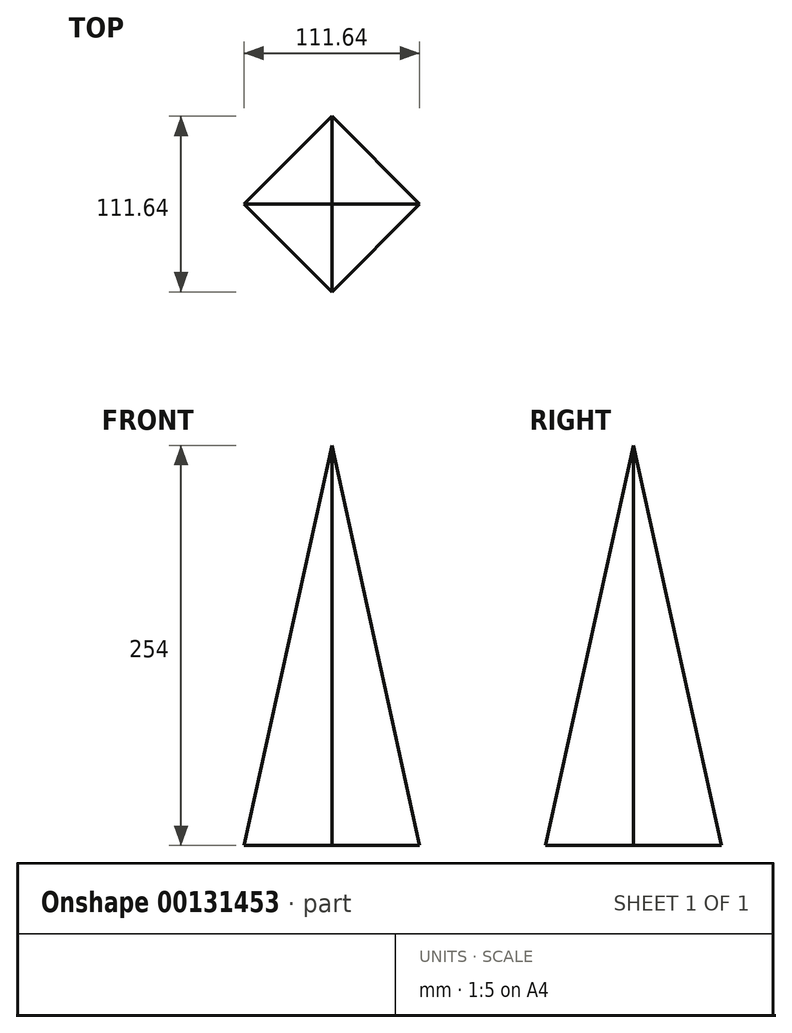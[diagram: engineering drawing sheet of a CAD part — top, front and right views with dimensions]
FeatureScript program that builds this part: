
annotation { "Feature Type Name" : "Feature", "Feature Type Description" : "" }
export const myFeature = defineFeature(function(context is Context, id is Id, definition is map)
    precondition{}
    {
        {
            var Q0;
            Q0=qCreatedBy(makeId("Top.planeOp"),FACE);
            var sketch = newSketch(context, id + "F0", { "sketchPlane" : qUnion([Q0])});
            skCircle(sketch, "E0.cCircle", {"center": v(0, 0) * mm, "radius": 55.82 * mm, "construction": true});
            skLineSegment(sketch, "E0.0", {"start": v(-55.82, 0) * mm, "end": v(0, 55.82) * mm});
            skLineSegment(sketch, "E0.1", {"start": v(0, 55.82) * mm, "end": v(55.82, 0) * mm});
            skLineSegment(sketch, "E0.2", {"start": v(55.82, 0) * mm, "end": v(0, -55.82) * mm});
            skLineSegment(sketch, "E0.3", {"start": v(0, -55.82) * mm, "end": v(-55.82, 0) * mm});
            skSolve(sketch);
        }
        {
            var Q0;
            Q0=qCreatedBy(makeId("Top.planeOp"),FACE);
            cPlane(context, id + "F1", {"entities" : qUnion([Q0]), "cplaneType" : CPlaneType.OFFSET, "offset" : 254 * mm, "width" : 152.4 * mm, "height" : 152.4 * mm});
        }
        {
            var Q0;
            Q0=qCreatedBy(id+"F1.planeOp",FACE);
            var sketch = newSketch(context, id + "F2", { "sketchPlane" : qUnion([Q0])});
            skPoint(sketch, "E1", {"position": v(0, 0) * mm});
            skSolve(sketch);
        }
        {
            var Q0;
            Q0=makeQuery(id+"F0.imprint","IMPRINT",FACE,{"disambiguationData":[TD([[makeQuery(id+"F0.imprint","IMPRINT",EDGE,{"derivedFrom":sQuery(id+"F0.wireOp",EDGE,"E0.0")}),-1.0]])]});
            var Q1;
            Q1=sQuery(id+"F2.wireOp",VERTEX,"E1");
            loft(context, id + "F3", {"sheetProfilesArray" : [{ "sheetProfileEntities" : qUnion([Q0]) }, { "sheetProfileEntities" : qUnion([Q1]) }]});
        }
    });
